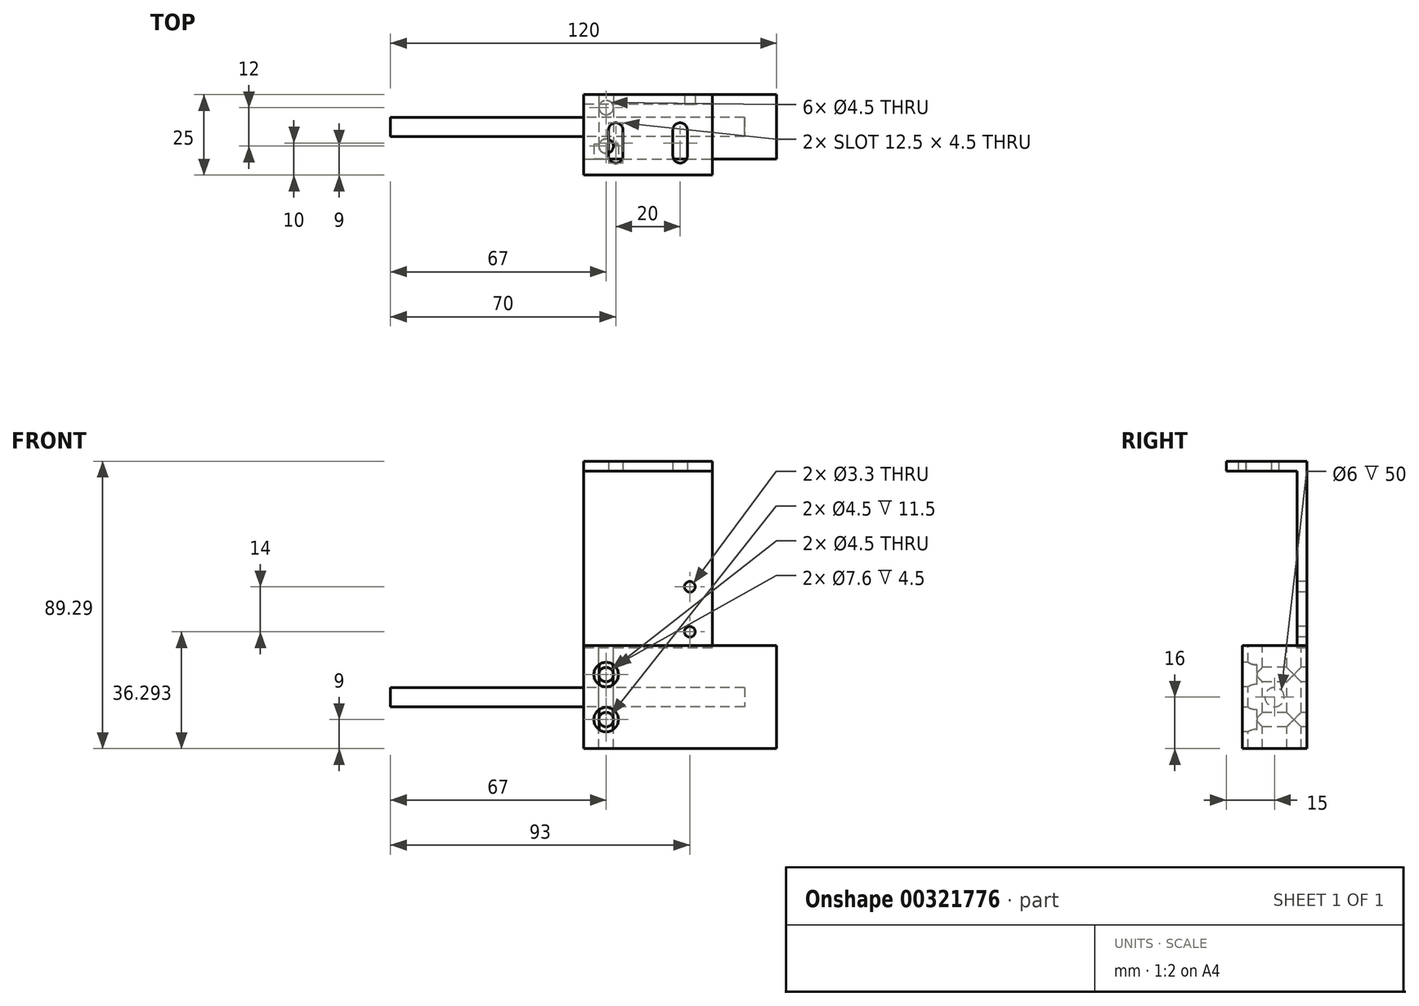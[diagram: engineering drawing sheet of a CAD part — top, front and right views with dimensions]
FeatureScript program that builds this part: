
annotation { "Feature Type Name" : "Feature", "Feature Type Description" : "" }
export const myFeature = defineFeature(function(context is Context, id is Id, definition is map)
    precondition{}
    {
        {
            var Q0;
            Q0=qCreatedBy(makeId("Front.planeOp"),FACE);
            var sketch = newSketch(context, id + "F0", { "sketchPlane" : qUnion([Q0])});
            skLineSegment(sketch, "E0.bottom", {"start": v(-39, 5.5) * mm, "end": v(21, 5.5) * mm});
            skLineSegment(sketch, "E0.top", {"start": v(-39, -26.5) * mm, "end": v(21, -26.5) * mm});
            skLineSegment(sketch, "E0.left", {"start": v(-39, 5.5) * mm, "end": v(-39, -26.5) * mm});
            skLineSegment(sketch, "E0.right", {"start": v(21, 5.5) * mm, "end": v(21, -26.5) * mm});
            skSolve(sketch);
        }
        {
            var Q0;
            Q0=qSketchRegion(id+"F0",true);
            extrude(context, id + "F1", {"entities" : qUnion([Q0]), "oppositeDirection" : true, "depth" : 20 * mm});
        }
        {
            var Q0;
            Q0=makeQuery(id+"F1.opExtrude","SWEPT_FACE",FACE,{"disambiguationData":[OSD([sQuery(id+"F0.wireOp",EDGE,"E0.left")])]});
            var sketch = newSketch(context, id + "F2", { "sketchPlane" : qUnion([Q0])});
            skPoint(sketch, "E1.centerSnap0", {"position": v(-10, 5.5) * mm});
            skCircle(sketch, "E2", {"center": v(-10, -10.5) * mm, "radius": 3 * mm});
            skSolve(sketch);
        }
        {
            var Q0;
            Q0=qSketchRegion(id+"F2",true);
            extrude(context, id + "F3", {"entities" : qUnion([Q0]), "depth" : 60 * mm});
        }
        {
            var Q0;
            Q0=makeQuery(id+"F1.opExtrude","CAP_FACE",FACE,{"disambiguationData":[OSD([sQuery(id+"F0.wireOp",EDGE,"E0.bottom"),sQuery(id+"F0.wireOp",EDGE,"E0.top"),sQuery(id+"F0.wireOp",EDGE,"E0.left"),sQuery(id+"F0.wireOp",EDGE,"E0.right")])],"isStart":true});
            var sketch = newSketch(context, id + "F4", { "sketchPlane" : qUnion([Q0])});
            skPoint(sketch, "E3", {"position": v(-32, -3.5) * mm});
            skPoint(sketch, "E4", {"position": v(-32, -17.5) * mm});
            skSolve(sketch);
        }
        {
            var Q0;
            Q0=sQuery(id+"F4.wireOp",VERTEX,"E3");
            var Q1;
            Q1=sQuery(id+"F4.wireOp",VERTEX,"E4");
            var Q2;
            Q2=makeQuery(id+"F1.opExtrude","SWEPT_BODY",BODY,{"disambiguationData":[OSD([sQuery(id+"F0.wireOp",EDGE,"E0.bottom"),sQuery(id+"F0.wireOp",EDGE,"E0.top"),sQuery(id+"F0.wireOp",EDGE,"E0.left"),sQuery(id+"F0.wireOp",EDGE,"E0.right")])]});
            hole(context, id + "F5", {"style" : HoleStyle.C_BORE, "endStyle" : HoleEndStyle.THROUGH, "holeDiameter" : 4.5 * mm, "cBoreDiameter" : 7.6 * mm, "cBoreDepth" : 4.5 * mm, "locations" : qUnion([Q0, Q1]), "scope" : qUnion([Q2]), "isTappedThrough" : true});
        }
        {
            var Q0;
            Q0=makeQuery(id+"F1.opExtrude","SWEPT_FACE",FACE,{"disambiguationData":[OSD([sQuery(id+"F0.wireOp",EDGE,"E0.left")])]});
            var sketch = newSketch(context, id + "F6", { "sketchPlane" : qUnion([Q0])});
            skLineSegment(sketch, "E5.bottom", {"start": v(-20, 4.8) * mm, "end": v(-17, 4.8) * mm});
            skLineSegment(sketch, "E5.left", {"start": v(-20, 4.8) * mm, "end": v(-20, 62.8) * mm});
            skLineSegment(sketch, "E5.right", {"start": v(-17, 4.8) * mm, "end": v(-17, 59.8) * mm});
            skLineSegment(sketch, "E6.top", {"start": v(-17, 59.8) * mm, "end": v(5, 59.8) * mm});
            skLineSegment(sketch, "E6.right", {"start": v(5, 62.8) * mm, "end": v(5, 59.8) * mm});
            skLineSegment(sketch, "E7", {"start": v(-20, 62.8) * mm, "end": v(5, 62.8) * mm});
            skSolve(sketch);
        }
        {
            var Q0;
            Q0=qSketchRegion(id+"F6",true);
            extrude(context, id + "F7", {"entities" : qUnion([Q0]), "oppositeDirection" : true, "depth" : 40 * mm});
        }
        {
            var Q0;
            Q0=makeQuery(id+"F7.opExtrude","SWEPT_FACE",FACE,{"disambiguationData":[OSD([sQuery(id+"F6.wireOp",EDGE,"E5.right")])]});
            var sketch = newSketch(context, id + "F8", { "sketchPlane" : qUnion([Q0])});
            skPoint(sketch, "E8", {"position": v(-6, 9.8) * mm});
            skPoint(sketch, "E9", {"position": v(-6, 23.8) * mm});
            skCircle(sketch, "E10", {"center": v(-6, 23.8) * mm, "radius": 2.25 * mm});
            skCircle(sketch, "E11", {"center": v(-6, 9.8) * mm, "radius": 2.25 * mm});
            skSolve(sketch);
        }
        {
            var Q0;
            Q0=makeQuery(id+"F1.opExtrude","SWEPT_FACE",FACE,{"disambiguationData":[OSD([sQuery(id+"F0.wireOp",EDGE,"E0.bottom")])]});
            var sketch = newSketch(context, id + "F9", { "sketchPlane" : qUnion([Q0])});
            skPoint(sketch, "E12", {"position": v(-32, 16) * mm});
            skPoint(sketch, "E13", {"position": v(-32, 4) * mm});
            skSolve(sketch);
        }
        {
            var Q0;
            Q0=sQuery(id+"F9.wireOp",VERTEX,"E12");
            var Q1;
            Q1=sQuery(id+"F9.wireOp",VERTEX,"E13");
            var Q2;
            Q2=makeQuery(id+"F1.opExtrude","SWEPT_BODY",BODY,{"disambiguationData":[OSD([sQuery(id+"F0.wireOp",EDGE,"E0.bottom"),sQuery(id+"F0.wireOp",EDGE,"E0.top"),sQuery(id+"F0.wireOp",EDGE,"E0.left"),sQuery(id+"F0.wireOp",EDGE,"E0.right")])]});
            hole(context, id + "F10", {"style" : HoleStyle.SIMPLE, "endStyle" : HoleEndStyle.THROUGH, "holeDiameter" : 4.5 * mm, "locations" : qUnion([Q0, Q1]), "scope" : qUnion([Q2]), "isTappedThrough" : true});
        }
        {
            var Q0;
            Q0=makeQuery(id+"F1.opExtrude","SWEPT_FACE",FACE,{"disambiguationData":[OSD([sQuery(id+"F0.wireOp",EDGE,"E0.left")])]});
            var sketch = newSketch(context, id + "F11", { "sketchPlane" : qUnion([Q0])});
            skCircle(sketch, "E14", {"center": v(-10, -10.5) * mm, "radius": 3 * mm});
            skPoint(sketch, "E14.centerSnap0", {"position": v(-10, 5.5) * mm});
            skPoint(sketch, "E14.centerSnap1", {"position": v(0, -10.5) * mm});
            skSolve(sketch);
        }
        {
            var Q0;
            Q0=qSketchRegion(id+"F11",true);
            extrude(context, id + "F12", {"entities" : qUnion([Q0]), "operationType" : NewBodyOperationType.REMOVE, "oppositeDirection" : true, "depth" : 50 * mm});
        }
        {
            var Q0;
            Q0=sQuery(id+"F8.wireOp",VERTEX,"E9");
            var Q1;
            Q1=sQuery(id+"F8.wireOp",VERTEX,"E8");
            var Q2;
            Q2=makeQuery(id+"F7.opExtrude","SWEPT_BODY",BODY,{"disambiguationData":[OSD([sQuery(id+"F6.wireOp",EDGE,"E5.bottom"),sQuery(id+"F6.wireOp",EDGE,"E5.left"),sQuery(id+"F6.wireOp",EDGE,"E5.right"),sQuery(id+"F6.wireOp",EDGE,"E6.top"),sQuery(id+"F6.wireOp",EDGE,"E6.right"),sQuery(id+"F6.wireOp",EDGE,"E7")])]});
            hole(context, id + "F13", {"style" : HoleStyle.SIMPLE, "endStyle" : HoleEndStyle.THROUGH, "standardTappedOrClearance" : lookupTablePath({ "standard" : "ISO", "engagement" : "75%", "pitch" : "0.7 mm", "size" : "M4", "type" : "Tapped" }), "standardBlindInLast" : lookupTablePath({ "standard" : "ISO", "engagement" : "75%", "pitch" : "0.7 mm", "size" : "M4", "type" : "Tapped" }), "holeDiameter" : 3.3 * mm, "startFromSketch" : true, "locations" : qUnion([Q0, Q1]), "scope" : qUnion([Q2]), "showTappedDepth" : true, "tappedDepth" : 12 * mm, "tapClearance" : 3, "majorDiameter" : 4 * mm});
        }
        {
            var Q0;
            Q0=makeQuery(id+"F7.opExtrude","SWEPT_FACE",FACE,{"disambiguationData":[OSD([sQuery(id+"F6.wireOp",EDGE,"E6.top")])]});
            var sketch = newSketch(context, id + "F14", { "sketchPlane" : qUnion([Q0])});
            skPoint(sketch, "E15.positionSnap0", {"position": v(-39, -6) * mm});
            skArc(sketch, "E16", {"start": v(-26.75, -1.06) * mm, "mid": v(-28.97, 1.25) * mm, "end": v(-31.25, -1) * mm});
            skArc(sketch, "E17", {"start": v(-31.25, -9) * mm, "mid": v(-29, -11.25) * mm, "end": v(-26.75, -9) * mm});
            skArc(sketch, "E18", {"start": v(-11.25, -9) * mm, "mid": v(-8.98, -11.25) * mm, "end": v(-6.75, -8.95) * mm});
            skArc(sketch, "E19", {"start": v(-6.75, -1.05) * mm, "mid": v(-8.99, 1.25) * mm, "end": v(-11.25, -1.03) * mm});
            skLineSegment(sketch, "E20", {"start": v(-31.25, -1) * mm, "end": v(-31.25, -9) * mm});
            skLineSegment(sketch, "E21", {"start": v(-26.75, -1.06) * mm, "end": v(-26.75, -9) * mm});
            skLineSegment(sketch, "E22", {"start": v(-11.25, -1.03) * mm, "end": v(-11.25, -9) * mm});
            skLineSegment(sketch, "E23", {"start": v(-6.75, -9.05) * mm, "end": v(-6.75, -1.05) * mm});
            skSolve(sketch);
        }
        {
            var Q0;
            Q0=qSketchRegion(id+"F14",true);
            extrude(context, id + "F15", {"entities" : qUnion([Q0]), "operationType" : NewBodyOperationType.REMOVE, "oppositeDirection" : true, "depth" : 25 * mm});
        }
    });
